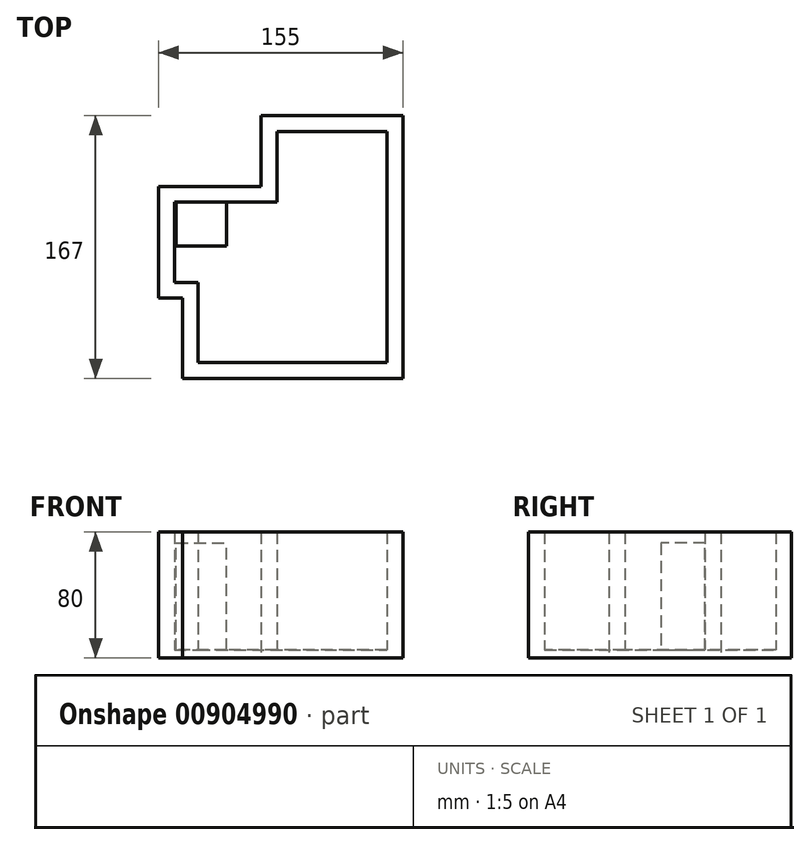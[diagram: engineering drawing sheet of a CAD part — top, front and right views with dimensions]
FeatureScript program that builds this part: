
annotation { "Feature Type Name" : "Feature", "Feature Type Description" : "" }
export const myFeature = defineFeature(function(context is Context, id is Id, definition is map)
    precondition{}
    {
        {
            var Q0;
            Q0=qCreatedBy(makeId("Top.planeOp"),FACE);
            var sketch = newSketch(context, id + "F0", { "sketchPlane" : qUnion([Q0])});
            skLineSegment(sketch, "E0", {"start": v(0, 0) * mm, "end": v(-70, 0) * mm});
            skLineSegment(sketch, "E1", {"start": v(-70, 0) * mm, "end": v(-70, -45) * mm});
            skLineSegment(sketch, "E2", {"start": v(-70, -45) * mm, "end": v(-135, -45) * mm});
            skLineSegment(sketch, "E3", {"start": v(-135, -45) * mm, "end": v(-135, -96) * mm});
            skLineSegment(sketch, "E4", {"start": v(-135, -96) * mm, "end": v(-120, -96) * mm});
            skLineSegment(sketch, "E5", {"start": v(-120, -96) * mm, "end": v(-120, -147) * mm});
            skLineSegment(sketch, "E6", {"start": v(-120, -147) * mm, "end": v(0, -147) * mm});
            skLineSegment(sketch, "E7", {"start": v(0, -147) * mm, "end": v(0, 0) * mm});
            skSolve(sketch);
        }
        {
            var Q0;
            Q0 = qSketchRegion(id + "F0", true);
            extrude(context, id + "F1", {"entities" : qUnion([Q0]), "depth" : 75 * mm, "offsetDistance" : 25 * mm});
        }
        {
            var Q0;
            Q0=makeQuery(id+"F1.opExtrude","CAP_FACE",FACE,{"disambiguationData":[OSD([sQuery(id+"F0.wireOp",EDGE,"E0"),sQuery(id+"F0.wireOp",EDGE,"E1"),sQuery(id+"F0.wireOp",EDGE,"E2"),sQuery(id+"F0.wireOp",EDGE,"E3"),sQuery(id+"F0.wireOp",EDGE,"E4"),sQuery(id+"F0.wireOp",EDGE,"E5"),sQuery(id+"F0.wireOp",EDGE,"E6"),sQuery(id+"F0.wireOp",EDGE,"E7")])],"isStart":false});
            shell(context, id + "F2", {"entities" : qUnion([Q0]), "thickness" : 0.01 * mm});
        }
        {
            var Q0;
            Q0=makeQuery(id+"F1.opExtrude","SWEPT_FACE",FACE,{"disambiguationData":[OSD([sQuery(id+"F0.wireOp",EDGE,"E2")])]});
            var sketch = newSketch(context, id + "F3", { "sketchPlane" : qUnion([Q0])});
            skLineSegment(sketch, "E8.bottom", {"start": v(134, 0) * mm, "end": v(102, 0) * mm});
            skLineSegment(sketch, "E8.top", {"start": v(134, 68) * mm, "end": v(102, 68) * mm});
            skLineSegment(sketch, "E8.left", {"start": v(134, 0) * mm, "end": v(134, 68) * mm});
            skLineSegment(sketch, "E8.right", {"start": v(102, 0) * mm, "end": v(102, 68) * mm});
            skSolve(sketch);
        }
        {
            var Q0;
            Q0=sQuery(id+"F3.wireOp",EDGE,"E8.bottom");
            var Q1;
            Q1=sQuery(id+"F3.wireOp",EDGE,"E8.top");
            var Q2;
            Q2=sQuery(id+"F3.wireOp",EDGE,"E8.right");
            var Q3;
            Q3=sQuery(id+"F3.wireOp",EDGE,"E8.left");
            extrude(context, id + "F4", {"bodyType" : ToolBodyType.SURFACE, "surfaceEntities" : qUnion([Q0, Q1, Q2, Q3]), "oppositeDirection" : true, "depth" : 28 * mm, "offsetDistance" : 25 * mm});
        }
        {
            var Q0;
            Q0=makeQuery(id+"F1.opExtrude","SWEPT_FACE",FACE,{"disambiguationData":[OSD([sQuery(id+"F0.wireOp",EDGE,"E7")])]});
            extrude(context, id + "F5", {"entities" : qUnion([Q0]), "operationType" : NewBodyOperationType.ADD, "depth" : 10 * mm, "offsetDistance" : 25 * mm});
        }
        {
            var Q0;
            {var subQ0=sQuery(id+"F0.wireOp",EDGE,"E0");Q0=makeQuery(id+"F5.boolean.opBoolean","MERGE",FACE,{"derivedFrom":[makeQuery(id+"F1.opExtrude","SWEPT_FACE",FACE,{"disambiguationData":[OSD([subQ0])]}),makeQuery(id+"F5.opExtrude","SWEPT_FACE",FACE,{"disambiguationData":[OSD([subQ0,sQuery(id+"F0.wireOp",EDGE,"E7")])]})]});}
            extrude(context, id + "F6", {"entities" : qUnion([Q0]), "operationType" : NewBodyOperationType.ADD, "depth" : 10 * mm, "offsetDistance" : 25 * mm});
        }
        {
            var Q0;
            {var subQ0=sQuery(id+"F0.wireOp",EDGE,"E1");Q0=makeQuery(id+"F6.boolean.opBoolean","MERGE",FACE,{"derivedFrom":[makeQuery(id+"F1.opExtrude","SWEPT_FACE",FACE,{"disambiguationData":[OSD([subQ0])]}),makeQuery(id+"F6.opExtrude","SWEPT_FACE",FACE,{"disambiguationData":[OSD([sQuery(id+"F0.wireOp",EDGE,"E0"),subQ0])]})]});}
            extrude(context, id + "F7", {"entities" : qUnion([Q0]), "operationType" : NewBodyOperationType.ADD, "depth" : 10 * mm, "offsetDistance" : 25 * mm});
        }
        {
            var Q0;
            Q0=makeQuery(id+"F1.opExtrude","SWEPT_FACE",FACE,{"disambiguationData":[OSD([sQuery(id+"F0.wireOp",EDGE,"E2")])]});
            extrude(context, id + "F8", {"entities" : qUnion([Q0]), "operationType" : NewBodyOperationType.ADD, "depth" : 10 * mm, "offsetDistance" : 25 * mm});
        }
        {
            var Q0;
            {var subQ0=sQuery(id+"F0.wireOp",EDGE,"E3");Q0=makeQuery(id+"F8.boolean.opBoolean","MERGE",FACE,{"derivedFrom":[makeQuery(id+"F1.opExtrude","SWEPT_FACE",FACE,{"disambiguationData":[OSD([subQ0])]}),makeQuery(id+"F8.opExtrude","SWEPT_FACE",FACE,{"disambiguationData":[OSD([sQuery(id+"F0.wireOp",EDGE,"E2"),subQ0])]})]});}
            extrude(context, id + "F9", {"entities" : qUnion([Q0]), "operationType" : NewBodyOperationType.ADD, "depth" : 10 * mm, "offsetDistance" : 25 * mm});
        }
        {
            var Q0;
            {var subQ0=sQuery(id+"F0.wireOp",EDGE,"E4");Q0=makeQuery(id+"F9.boolean.opBoolean","MERGE",FACE,{"derivedFrom":[makeQuery(id+"F1.opExtrude","SWEPT_FACE",FACE,{"disambiguationData":[OSD([subQ0])]}),makeQuery(id+"F9.opExtrude","SWEPT_FACE",FACE,{"disambiguationData":[OSD([sQuery(id+"F0.wireOp",EDGE,"E3"),subQ0])]})]});}
            extrude(context, id + "F10", {"entities" : qUnion([Q0]), "operationType" : NewBodyOperationType.ADD, "depth" : 10 * mm, "offsetDistance" : 25 * mm});
        }
        {
            var Q0;
            Q0=makeQuery(id+"F1.opExtrude","SWEPT_FACE",FACE,{"disambiguationData":[OSD([sQuery(id+"F0.wireOp",EDGE,"E5")])]});
            extrude(context, id + "F11", {"entities" : qUnion([Q0]), "operationType" : NewBodyOperationType.ADD, "depth" : 10 * mm, "offsetDistance" : 25 * mm});
        }
        {
            var Q0;
            {var subQ0=sQuery(id+"F0.wireOp",EDGE,"E6");Q0=makeQuery(id+"F11.boolean.opBoolean","MERGE",FACE,{"derivedFrom":[makeQuery(id+"F5.boolean.opBoolean","MERGE",FACE,{"derivedFrom":[makeQuery(id+"F1.opExtrude","SWEPT_FACE",FACE,{"disambiguationData":[OSD([subQ0])]}),makeQuery(id+"F5.opExtrude","SWEPT_FACE",FACE,{"disambiguationData":[OSD([subQ0,sQuery(id+"F0.wireOp",EDGE,"E7")])]})]}),makeQuery(id+"F11.opExtrude","SWEPT_FACE",FACE,{"disambiguationData":[OSD([sQuery(id+"F0.wireOp",EDGE,"E5"),subQ0])]})]});}
            extrude(context, id + "F12", {"entities" : qUnion([Q0]), "operationType" : NewBodyOperationType.ADD, "depth" : 10 * mm, "offsetDistance" : 25 * mm});
        }
        {
            var Q0;
            {var subQ0=sQuery(id+"F0.wireOp",EDGE,"E6");var subQ1=sQuery(id+"F0.wireOp",EDGE,"E5");var subQ2=sQuery(id+"F0.wireOp",EDGE,"E7");var subQ3=sQuery(id+"F0.wireOp",EDGE,"E4");var subQ4=sQuery(id+"F0.wireOp",EDGE,"E3");var subQ5=sQuery(id+"F0.wireOp",EDGE,"E2");var subQ6=sQuery(id+"F0.wireOp",EDGE,"E1");var subQ7=sQuery(id+"F0.wireOp",EDGE,"E0");Q0=makeQuery(id+"F12.boolean.opBoolean","MERGE",FACE,{"derivedFrom":[makeQuery(id+"F11.boolean.opBoolean","MERGE",FACE,{"derivedFrom":[makeQuery(id+"F10.boolean.opBoolean","MERGE",FACE,{"derivedFrom":[makeQuery(id+"F9.boolean.opBoolean","MERGE",FACE,{"derivedFrom":[makeQuery(id+"F8.boolean.opBoolean","MERGE",FACE,{"derivedFrom":[makeQuery(id+"F7.boolean.opBoolean","MERGE",FACE,{"derivedFrom":[makeQuery(id+"F6.boolean.opBoolean","MERGE",FACE,{"derivedFrom":[makeQuery(id+"F5.boolean.opBoolean","MERGE",FACE,{"derivedFrom":[makeQuery(id+"F1.opExtrude","CAP_FACE",FACE,{"disambiguationData":[OSD([subQ7,subQ6,subQ5,subQ4,subQ3,subQ1,subQ0,subQ2])],"isStart":true}),makeQuery(id+"F5.opExtrude","SWEPT_FACE",FACE,{"disambiguationData":[OSD([subQ2]),TDD([makeQuery(id+"F1.opExtrude","CAP_EDGE",EDGE,{"disambiguationData":[OSD([subQ2])],"isStart":true})])]})]}),makeQuery(id+"F6.opExtrude","SWEPT_FACE",FACE,{"disambiguationData":[OSD([subQ7,subQ2]),TDD([makeQuery(id+"F5.boolean.opBoolean","MERGE",EDGE,{"derivedFrom":[makeQuery(id+"F1.opExtrude","CAP_EDGE",EDGE,{"disambiguationData":[OSD([subQ7])],"isStart":true}),makeQuery(id+"F5.opExtrude","SWEPT_EDGE",EDGE,{"disambiguationData":[OSD([subQ7,subQ2]),TDD([makeQuery(id+"F1.opExtrude","CAP_VERTEX",VERTEX,{"disambiguationData":[OSD([subQ7,subQ2])],"isStart":true})])]})]})])]})]}),makeQuery(id+"F7.opExtrude","SWEPT_FACE",FACE,{"disambiguationData":[OSD([subQ7,subQ6]),TDD([makeQuery(id+"F6.boolean.opBoolean","MERGE",EDGE,{"derivedFrom":[makeQuery(id+"F1.opExtrude","CAP_EDGE",EDGE,{"disambiguationData":[OSD([subQ6])],"isStart":true}),makeQuery(id+"F6.opExtrude","SWEPT_EDGE",EDGE,{"disambiguationData":[OSD([subQ7,subQ6]),TDD([makeQuery(id+"F1.opExtrude","CAP_VERTEX",VERTEX,{"disambiguationData":[OSD([subQ7,subQ6])],"isStart":true})])]})]})])]})]}),makeQuery(id+"F8.opExtrude","SWEPT_FACE",FACE,{"disambiguationData":[OSD([subQ5]),TDD([makeQuery(id+"F1.opExtrude","CAP_EDGE",EDGE,{"disambiguationData":[OSD([subQ5])],"isStart":true})])]})]}),makeQuery(id+"F9.opExtrude","SWEPT_FACE",FACE,{"disambiguationData":[OSD([subQ5,subQ4]),TDD([makeQuery(id+"F8.boolean.opBoolean","MERGE",EDGE,{"derivedFrom":[makeQuery(id+"F1.opExtrude","CAP_EDGE",EDGE,{"disambiguationData":[OSD([subQ4])],"isStart":true}),makeQuery(id+"F8.opExtrude","SWEPT_EDGE",EDGE,{"disambiguationData":[OSD([subQ5,subQ4]),TDD([makeQuery(id+"F1.opExtrude","CAP_VERTEX",VERTEX,{"disambiguationData":[OSD([subQ5,subQ4])],"isStart":true})])]})]})])]})]}),makeQuery(id+"F10.opExtrude","SWEPT_FACE",FACE,{"disambiguationData":[OSD([subQ4,subQ3]),TDD([makeQuery(id+"F9.boolean.opBoolean","MERGE",EDGE,{"derivedFrom":[makeQuery(id+"F1.opExtrude","CAP_EDGE",EDGE,{"disambiguationData":[OSD([subQ3])],"isStart":true}),makeQuery(id+"F9.opExtrude","SWEPT_EDGE",EDGE,{"disambiguationData":[OSD([subQ4,subQ3]),TDD([makeQuery(id+"F1.opExtrude","CAP_VERTEX",VERTEX,{"disambiguationData":[OSD([subQ4,subQ3])],"isStart":true})])]})]})])]})]}),makeQuery(id+"F11.opExtrude","SWEPT_FACE",FACE,{"disambiguationData":[OSD([subQ1]),TDD([makeQuery(id+"F1.opExtrude","CAP_EDGE",EDGE,{"disambiguationData":[OSD([subQ1])],"isStart":true})])]})]}),makeQuery(id+"F12.opExtrude","SWEPT_FACE",FACE,{"disambiguationData":[OSD([subQ1,subQ0,subQ2]),TDD([makeQuery(id+"F11.boolean.opBoolean","MERGE",EDGE,{"derivedFrom":[makeQuery(id+"F5.boolean.opBoolean","MERGE",EDGE,{"derivedFrom":[makeQuery(id+"F1.opExtrude","CAP_EDGE",EDGE,{"disambiguationData":[OSD([subQ0])],"isStart":true}),makeQuery(id+"F5.opExtrude","SWEPT_EDGE",EDGE,{"disambiguationData":[OSD([subQ0,subQ2]),TDD([makeQuery(id+"F1.opExtrude","CAP_VERTEX",VERTEX,{"disambiguationData":[OSD([subQ0,subQ2])],"isStart":true})])]})]}),makeQuery(id+"F11.opExtrude","SWEPT_EDGE",EDGE,{"disambiguationData":[OSD([subQ1,subQ0]),TDD([makeQuery(id+"F1.opExtrude","CAP_VERTEX",VERTEX,{"disambiguationData":[OSD([subQ1,subQ0])],"isStart":true})])]})]})])]})]});}
            extrude(context, id + "F13", {"entities" : qUnion([Q0]), "operationType" : NewBodyOperationType.ADD, "depth" : 5 * mm, "offsetDistance" : 25 * mm});
        }
        {
            var Q0;
            Q0=makeQuery(id+"F4.opExtrude","SWEPT_FACE",FACE,{"disambiguationData":[OSD([sQuery(id+"F3.wireOp",EDGE,"E8.bottom")])]});
            extrude(context, id + "F14", {"entities" : qUnion([Q0]), "operationType" : NewBodyOperationType.ADD, "endBound" : BoundingType.UP_TO_NEXT, "oppositeDirection" : true, "depth" : 25 * mm, "offsetDistance" : 25 * mm});
        }
        {
            var Q0;
            Q0=makeQuery(id+"F4.opExtrude","SWEPT_FACE",FACE,{"disambiguationData":[OSD([sQuery(id+"F3.wireOp",EDGE,"E8.bottom")])]});
            extrude(context, id + "F15", {"entities" : qUnion([Q0]), "operationType" : NewBodyOperationType.ADD, "oppositeDirection" : true, "depth" : 68 * mm, "offsetDistance" : 25 * mm});
        }
    });
